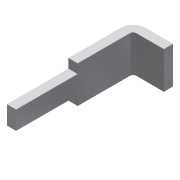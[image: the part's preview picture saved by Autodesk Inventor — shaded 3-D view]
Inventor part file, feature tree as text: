
AUTODESK INVENTOR PART (.ipt)
format: ipt  version: 2014 (Build 180170000, 170)  size: 92,672 bytes
history: native  units: in
note: dims shown in document units (in); Inventor stores cm internally (conversion verified against a paired STEP export)
features: other x3, sketch x2
ambient origin geometry x8: Origin, YZ Plane, XZ Plane, XY Plane, X Axis, Y Axis, Z Axis, Center Point
bodies: Solid1 (feature_tree)
feature tree (5):
  other  "pins_encoder body.ipt"
  other  "Solid1::pins_encoder body.ipt"
  other  "TaggingFeature1"
  sketch  "Sketch2"  dims[d0=0.3937in]
  sketch  "Sketch3"  dims[d2=0.015in d3=0.09in d4=0.005in d6=0.02in d7=0.06in d8=0.0in d9=0.03in d11=0.015in d12=0.1in d14=0.0in d10=0.06in]
